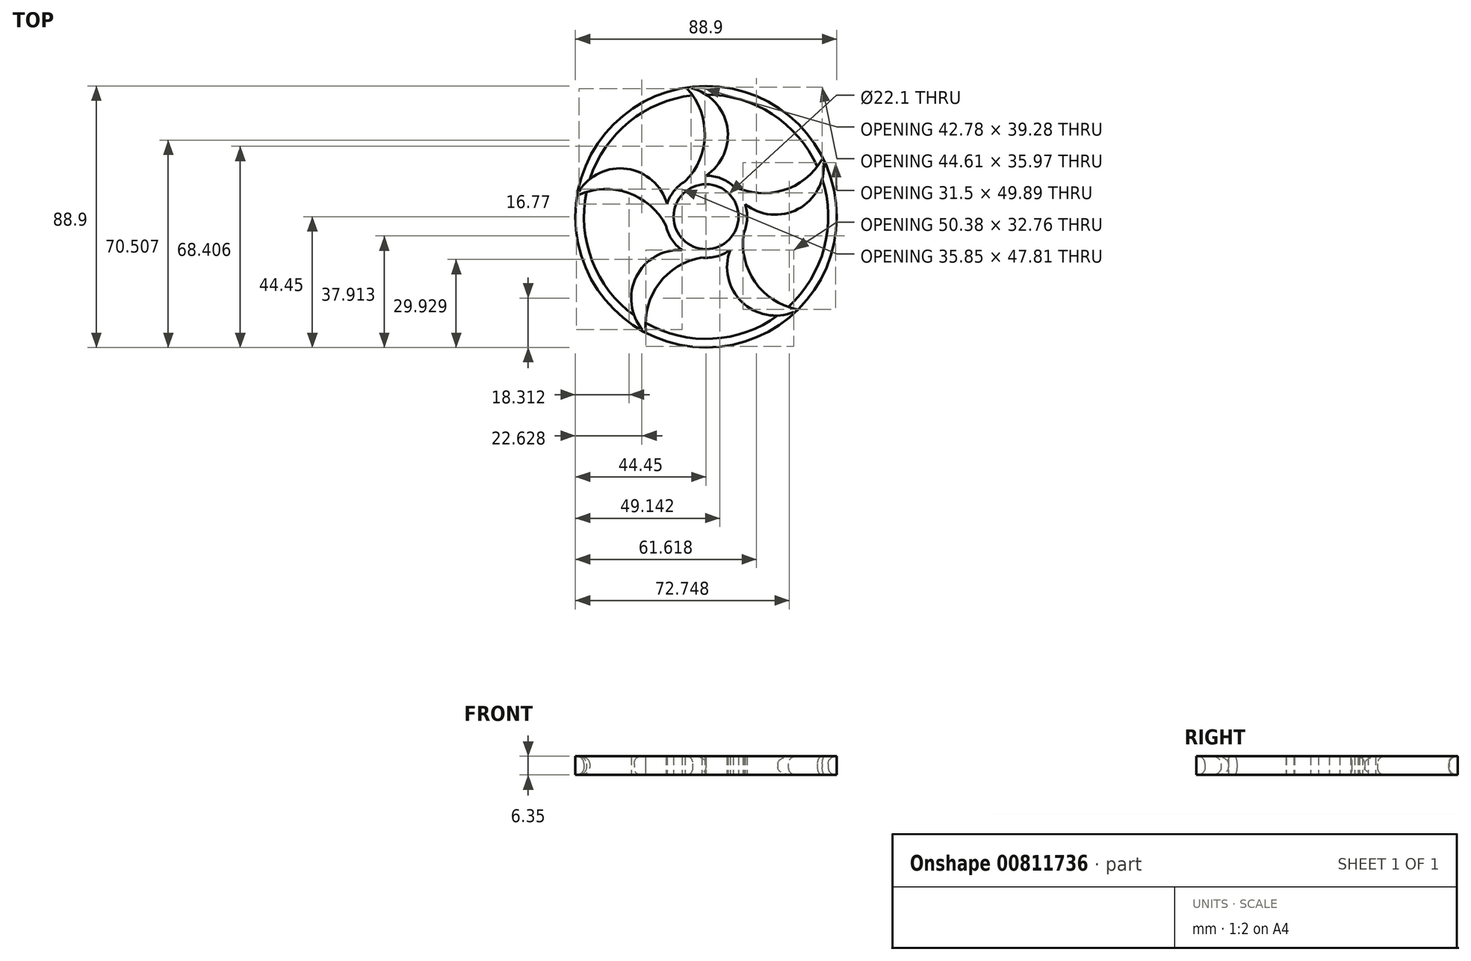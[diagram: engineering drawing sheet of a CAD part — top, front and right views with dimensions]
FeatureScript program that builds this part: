
annotation { "Feature Type Name" : "Feature", "Feature Type Description" : "" }
export const myFeature = defineFeature(function(context is Context, id is Id, definition is map)
    precondition{}
    {
        {
            var Q0;
            Q0=qCreatedBy(makeId("Top.planeOp"),FACE);
            var sketch = newSketch(context, id + "F0", { "sketchPlane" : qUnion([Q0])});
            skPoint(sketch, "E0.center", {"position": v(0, 0) * mm});
            skLineSegment(sketch, "E1", {"start": v(12.1, 6.99) * mm, "end": v(12.1, 6.99) * mm});
            skCircle(sketch, "E2", {"center": v(0, 0) * mm, "radius": 44.45 * mm});
            skCircle(sketch, "E3", {"center": v(0, 0) * mm, "radius": 11.05 * mm});
            skArc(sketch, "E4", {"start": v(-4.58, 41.28) * mm, "mid": v(-26.23, 32.2) * mm, "end": v(-39.5, 12.83) * mm});
            skArc(sketch, "E5", {"start": v(0, 13.97) * mm, "mid": v(7.43, 27.75) * mm, "end": v(0, 41.53) * mm});
            skArc(sketch, "E6.1.0", {"start": v(-13.29, 4.32) * mm, "mid": v(-24.1, 15.64) * mm, "end": v(-39.5, 12.83) * mm});
            skArc(sketch, "E6.2.0", {"start": v(-8.21, -11.3) * mm, "mid": v(-22.32, -18.08) * mm, "end": v(-24.41, -33.6) * mm});
            skArc(sketch, "E6.3.0", {"start": v(8.21, -11.3) * mm, "mid": v(10.3, -26.82) * mm, "end": v(24.41, -33.6) * mm});
            skArc(sketch, "E6.4.0", {"start": v(13.29, 4.32) * mm, "mid": v(28.69, 1.51) * mm, "end": v(39.5, 12.83) * mm});
            skArc(sketch, "E7.trimOffspring", {"start": v(-7.07, 12.05) * mm, "mid": v(-0.5, 26.2) * mm, "end": v(-4.58, 41.28) * mm});
            skArc(sketch, "E8.1.0", {"start": v(-13.64, -3) * mm, "mid": v(-25.08, 7.61) * mm, "end": v(-40.67, 8.4) * mm});
            skArc(sketch, "E8.2.0", {"start": v(-1.36, -13.9) * mm, "mid": v(-15, -21.5) * mm, "end": v(-20.56, -36.08) * mm});
            skArc(sketch, "E8.3.0", {"start": v(12.8, -5.59) * mm, "mid": v(15.82, -20.9) * mm, "end": v(27.96, -30.7) * mm});
            skArc(sketch, "E8.4.0", {"start": v(9.27, 10.45) * mm, "mid": v(24.77, 8.58) * mm, "end": v(37.84, 17.1) * mm});
            skArc(sketch, "E9.trimOffspring", {"start": v(-13.64, -3) * mm, "mid": v(-11.69, -7.65) * mm, "end": v(-8.21, -11.3) * mm});
            skArc(sketch, "E10", {"start": v(-7.07, 12.05) * mm, "mid": v(-10.89, 8.75) * mm, "end": v(-13.29, 4.32) * mm});
            skArc(sketch, "E11.trimOffspring", {"start": v(-1.36, -13.9) * mm, "mid": v(3.67, -13.48) * mm, "end": v(8.21, -11.3) * mm});
            skArc(sketch, "E12.trimOffspring", {"start": v(12.8, -5.59) * mm, "mid": v(13.95, -0.68) * mm, "end": v(13.29, 4.32) * mm});
            skArc(sketch, "E13.trimOffspring", {"start": v(-40.67, 8.4) * mm, "mid": v(-38.73, -15) * mm, "end": v(-24.41, -33.6) * mm});
            skArc(sketch, "E14.trimOffspring", {"start": v(-20.56, -36.08) * mm, "mid": v(2.3, -41.47) * mm, "end": v(24.41, -33.6) * mm});
            skArc(sketch, "E15.trimOffspring", {"start": v(27.96, -30.7) * mm, "mid": v(40.14, -10.63) * mm, "end": v(39.5, 12.83) * mm});
            skArc(sketch, "E16.trimOffspring", {"start": v(37.84, 17.1) * mm, "mid": v(22.52, 34.9) * mm, "end": v(0, 41.53) * mm});
            skArc(sketch, "E17.trimOffspring", {"start": v(9.27, 10.45) * mm, "mid": v(4.96, 13.06) * mm, "end": v(0, 13.97) * mm});
            skSolve(sketch);
        }
        {
            var Q0;
            Q0 = qSketchRegion(id + "F0", true);
            extrude(context, id + "F1", {"entities" : qUnion([Q0]), "depth" : 6.35 * mm, "offsetDistance" : 25.4 * mm});
        }
        {
            var Q0;
            Q0=makeQuery(id+"F1.opExtrude","CAP_EDGE",EDGE,{"disambiguationData":[OSD([sQuery(id+"F0.wireOp",EDGE,"E13.trimOffspring")])],"isStart":false});
            var Q1;
            Q1=makeQuery(id+"F1.opExtrude","CAP_EDGE",EDGE,{"disambiguationData":[OSD([sQuery(id+"F0.wireOp",EDGE,"E4")])],"isStart":false});
            var Q2;
            Q2=makeQuery(id+"F1.opExtrude","CAP_EDGE",EDGE,{"disambiguationData":[OSD([sQuery(id+"F0.wireOp",EDGE,"E16.trimOffspring")])],"isStart":false});
            var Q3;
            Q3=makeQuery(id+"F1.opExtrude","CAP_EDGE",EDGE,{"disambiguationData":[OSD([sQuery(id+"F0.wireOp",EDGE,"E15.trimOffspring")])],"isStart":false});
            var Q4;
            Q4=makeQuery(id+"F1.opExtrude","CAP_EDGE",EDGE,{"disambiguationData":[OSD([sQuery(id+"F0.wireOp",EDGE,"E14.trimOffspring")])],"isStart":false});
            fillet(context, id + "F2", {"entities" : qUnion([Q0, Q1, Q2, Q3, Q4]), "radius" : 2.54 * mm, "tangentPropagation" : true, "allowEdgeOverflow" : false});
        }
        {
            var Q0;
            Q0=makeQuery(id+"F1.opExtrude","CAP_EDGE",EDGE,{"disambiguationData":[OSD([sQuery(id+"F0.wireOp",EDGE,"E14.trimOffspring")])],"isStart":true});
            var Q1;
            Q1=makeQuery(id+"F1.opExtrude","CAP_EDGE",EDGE,{"disambiguationData":[OSD([sQuery(id+"F0.wireOp",EDGE,"E15.trimOffspring")])],"isStart":true});
            var Q2;
            Q2=makeQuery(id+"F1.opExtrude","CAP_EDGE",EDGE,{"disambiguationData":[OSD([sQuery(id+"F0.wireOp",EDGE,"E16.trimOffspring")])],"isStart":true});
            var Q3;
            Q3=makeQuery(id+"F1.opExtrude","CAP_EDGE",EDGE,{"disambiguationData":[OSD([sQuery(id+"F0.wireOp",EDGE,"E4")])],"isStart":true});
            var Q4;
            Q4=makeQuery(id+"F1.opExtrude","CAP_EDGE",EDGE,{"disambiguationData":[OSD([sQuery(id+"F0.wireOp",EDGE,"E13.trimOffspring")])],"isStart":true});
            fillet(context, id + "F3", {"entities" : qUnion([Q0, Q1, Q2, Q3, Q4]), "radius" : 2.54 * mm, "tangentPropagation" : true, "allowEdgeOverflow" : false});
        }
    });
